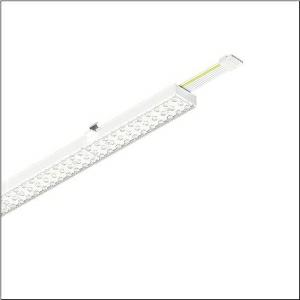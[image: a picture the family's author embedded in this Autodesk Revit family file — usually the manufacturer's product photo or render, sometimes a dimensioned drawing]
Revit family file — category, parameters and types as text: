
# Revit family: trunking_flex_31_51re12dc49b007
name_source: partatom
category: Lighting Fixtures
units: mm (PartAtom-declared; Revit-internal decimal feet)

## family parameters
Cut with Voids When Loaded = No
Host = Face
Light Source = No
Part Type = Normal
Room Calculation Point = No
Round Connector Dimension = Use Diameter
Shared = No

## types (1)
- Trunking Flex 31 (1 x LED, 8900 lm, 53 W, 4000K)
    Apparent Load = 53 VA
    CIE Flux Codes = 65 91 98 99 100
    Color Rendering = 80
    Color Temperature = 4000K
    Default Elevation = 1800 mm
    Description = Trunking Flex 31, luminaire insert, of extruded aluminium section, coated, traffic white (RAL 9016), length: 1.438mm, width: 91mm, height: 53mm, LED rated luminous flux: 8.900lm, light colour: 840, control gear: DALI 2, with system connector: socket, through-wiring: 7x 2.5mm², mains connection: 220..240V, AC, 50/60Hz, rated input power: 53W, primary light control with lens, of plastic, primary optical cover: cover, of PMMA, light emission: direct distribution, protection rating (complete): IP20, insulation class (complete): insulation class I (protective earthing), certification: CE, UKCA, impact resistance: IK02, permissible ambient temperature for indoor applications: -20..+40°C, packaging unit: 1 piece
    Height = 58 mm
    Lamp = 1 x LED
    Lamp Light Flux = 8900 lm
    Lamp Power = 53 W
    Lamp count = 1
    Length = 1438 mm
    Luminous efficacy = 168 lm/W
    Manufacturer = Siteco
    ModVariant = No
    Model = 51RE12DC49B007
    Mounting Place = Ceiling
    Mounting Type = Pendant
    Number of Poles = 1
    OnlyDefault = Yes
    Power Factor = 1
    Product Name = Trunking Flex 31
    Product group = luminaire insert
    ProductGroupID = 902
    Protection Class = Protection class I
    Protection Degree = IP 20
    RLX_Detail_Level = 1
    RLX_Emergency_Light_Flux = 0 lm
    RLX_Emergency_Type = 0
    RLX_Emergency_Type_DB = No
    RlxData = <blob elided: 22185 chars, md5=59eb3f0e>
    Socket = socket
    Standby Power = 0 W
    System Light Flux = 8900 lm
    System Power = 53 W
    Type Comments = Product without accessories
    Type Image = l_1297860.jpg
    URL = http://relux.com
    VarID = ---
    Voltage = 0 V
    Weight = 0.00 kg
    Width = 65 mm

## geometry (parser evidence)
native form markers: Blend x4, Sweep x11
no freeform markers — native parametric forms only
